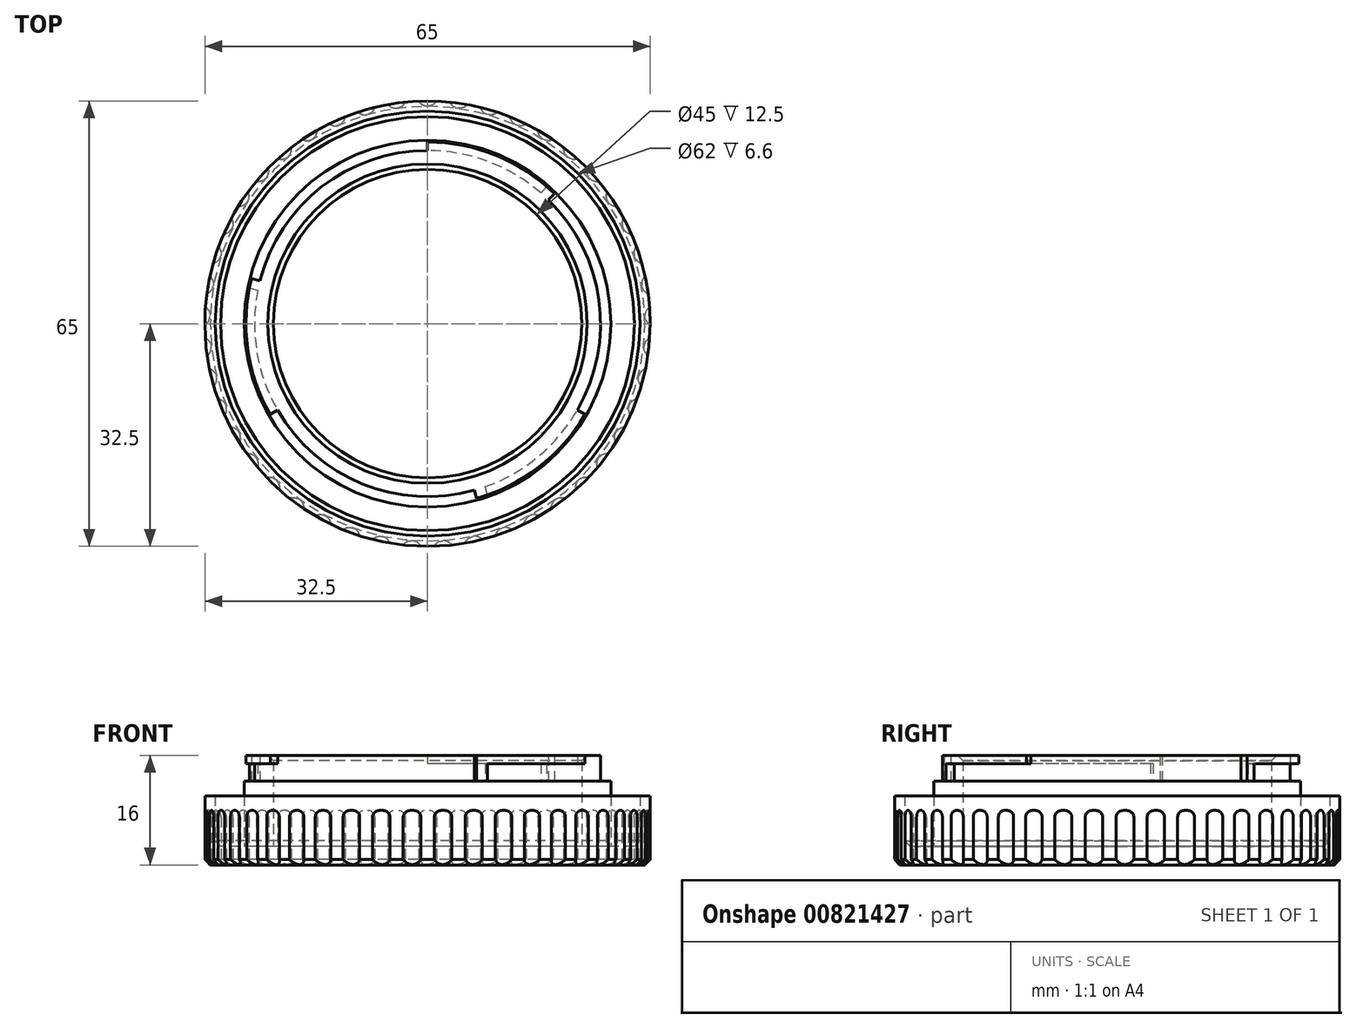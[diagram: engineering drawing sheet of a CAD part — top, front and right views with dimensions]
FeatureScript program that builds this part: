
annotation { "Feature Type Name" : "Feature", "Feature Type Description" : "" }
export const myFeature = defineFeature(function(context is Context, id is Id, definition is map)
    precondition{}
    {
        {
            var Q0;
            Q0=qCreatedBy(makeId("Top.planeOp"),FACE);
            var sketch = newSketch(context, id + "F0", { "sketchPlane" : qUnion([Q0])});
            skCircle(sketch, "E0", {"center": v(0, 0) * mm, "radius": 32.5 * mm});
            skCircle(sketch, "E1", {"center": v(0, 0) * mm, "radius": 31 * mm});
            skCircle(sketch, "E2", {"center": v(0, 0) * mm, "radius": 26.75 * mm});
            skCircle(sketch, "E3", {"center": v(0, 0) * mm, "radius": 25.25 * mm});
            skCircle(sketch, "E4", {"center": v(0, 0) * mm, "radius": 22.5 * mm});
            skCircle(sketch, "E5", {"center": v(0, 0) * mm, "radius": 26.5 * mm});
            skLineSegment(sketch, "E6", {"start": v(0, -3.47) * mm, "end": v(0, 43.61) * mm, "construction": true});
            skLineSegment(sketch, "E7", {"start": v(0, 26.5) * mm, "end": v(0, 25.25) * mm, "construction": true});
            skLineSegment(sketch, "E8", {"start": v(0, 0) * mm, "end": v(34.45, 35.25) * mm, "construction": true});
            skLineSegment(sketch, "E9", {"start": v(18.52, 18.95) * mm, "end": v(17.65, 18.06) * mm});
            skLineSegment(sketch, "E10.1.0", {"start": v(3, 1.74) * mm, "end": v(-37.77, -21.8) * mm, "construction": true});
            skLineSegment(sketch, "E10.1.1", {"start": v(0, 0) * mm, "end": v(-47.75, 12.2) * mm, "construction": true});
            skLineSegment(sketch, "E10.2.0", {"start": v(-3, 1.74) * mm, "end": v(37.77, -21.8) * mm, "construction": true});
            skLineSegment(sketch, "E10.2.1", {"start": v(0, 0) * mm, "end": v(13.3, -47.46) * mm, "construction": true});
            skLineSegment(sketch, "E11", {"start": v(-25.67, 6.56) * mm, "end": v(-24.46, 6.25) * mm});
            skLineSegment(sketch, "E12", {"start": v(-22.95, -13.25) * mm, "end": v(-21.87, -12.62) * mm});
            skLineSegment(sketch, "E13", {"start": v(6.82, -24.31) * mm, "end": v(7.15, -25.52) * mm});
            skLineSegment(sketch, "E14", {"start": v(21.87, -12.63) * mm, "end": v(22.95, -13.25) * mm});
            skCircle(sketch, "E15", {"center": v(0, 33.28) * mm, "radius": 1.52 * mm});
            skCircle(sketch, "E16.1.0", {"center": v(-4.63, 32.95) * mm, "radius": 1.52 * mm});
            skCircle(sketch, "E16.2.0", {"center": v(-9.17, 31.99) * mm, "radius": 1.52 * mm});
            skCircle(sketch, "E16.3.0", {"center": v(-13.53, 30.4) * mm, "radius": 1.52 * mm});
            skCircle(sketch, "E16.4.0", {"center": v(-17.63, 28.22) * mm, "radius": 1.52 * mm});
            skCircle(sketch, "E16.5.0", {"center": v(-21.39, 25.5) * mm, "radius": 1.52 * mm});
            skCircle(sketch, "E16.6.0", {"center": v(-24.73, 22.27) * mm, "radius": 1.52 * mm});
            skCircle(sketch, "E16.7.0", {"center": v(-27.59, 18.6) * mm, "radius": 1.52 * mm});
            skCircle(sketch, "E16.8.0", {"center": v(-29.9, 14.59) * mm, "radius": 1.52 * mm});
            skCircle(sketch, "E16.9.0", {"center": v(-31.65, 10.28) * mm, "radius": 1.52 * mm});
            skCircle(sketch, "E16.10.0", {"center": v(-32.77, 5.78) * mm, "radius": 1.52 * mm});
            skCircle(sketch, "E16.11.0", {"center": v(-33.26, 1.16) * mm, "radius": 1.52 * mm});
            skCircle(sketch, "E16.12.0", {"center": v(-33.1, -3.48) * mm, "radius": 1.52 * mm});
            skCircle(sketch, "E16.13.0", {"center": v(-32.29, -8.05) * mm, "radius": 1.52 * mm});
            skCircle(sketch, "E16.14.0", {"center": v(-30.85, -12.47) * mm, "radius": 1.52 * mm});
            skCircle(sketch, "E16.15.0", {"center": v(-28.82, -16.64) * mm, "radius": 1.52 * mm});
            skCircle(sketch, "E16.16.0", {"center": v(-26.22, -20.49) * mm, "radius": 1.52 * mm});
            skCircle(sketch, "E16.17.0", {"center": v(-23.12, -23.94) * mm, "radius": 1.52 * mm});
            skCircle(sketch, "E16.18.0", {"center": v(-19.56, -26.92) * mm, "radius": 1.52 * mm});
            skCircle(sketch, "E16.19.0", {"center": v(-15.62, -29.38) * mm, "radius": 1.52 * mm});
            skCircle(sketch, "E16.20.0", {"center": v(-11.38, -31.27) * mm, "radius": 1.52 * mm});
            skCircle(sketch, "E16.21.0", {"center": v(-6.92, -32.55) * mm, "radius": 1.52 * mm});
            skCircle(sketch, "E16.22.0", {"center": v(-2.32, -33.2) * mm, "radius": 1.52 * mm});
            skCircle(sketch, "E16.23.0", {"center": v(2.32, -33.2) * mm, "radius": 1.52 * mm});
            skCircle(sketch, "E16.24.0", {"center": v(6.92, -32.55) * mm, "radius": 1.52 * mm});
            skCircle(sketch, "E16.25.0", {"center": v(11.38, -31.27) * mm, "radius": 1.52 * mm});
            skCircle(sketch, "E16.26.0", {"center": v(15.62, -29.38) * mm, "radius": 1.52 * mm});
            skCircle(sketch, "E16.27.0", {"center": v(19.56, -26.92) * mm, "radius": 1.52 * mm});
            skCircle(sketch, "E16.28.0", {"center": v(23.12, -23.94) * mm, "radius": 1.52 * mm});
            skCircle(sketch, "E16.29.0", {"center": v(26.22, -20.49) * mm, "radius": 1.52 * mm});
            skCircle(sketch, "E16.30.0", {"center": v(28.82, -16.64) * mm, "radius": 1.52 * mm});
            skCircle(sketch, "E16.31.0", {"center": v(30.85, -12.47) * mm, "radius": 1.52 * mm});
            skCircle(sketch, "E16.32.0", {"center": v(32.29, -8.05) * mm, "radius": 1.52 * mm});
            skCircle(sketch, "E16.33.0", {"center": v(33.1, -3.48) * mm, "radius": 1.52 * mm});
            skCircle(sketch, "E16.34.0", {"center": v(33.26, 1.16) * mm, "radius": 1.52 * mm});
            skCircle(sketch, "E16.35.0", {"center": v(32.77, 5.78) * mm, "radius": 1.52 * mm});
            skCircle(sketch, "E16.36.0", {"center": v(31.65, 10.28) * mm, "radius": 1.52 * mm});
            skCircle(sketch, "E16.37.0", {"center": v(29.9, 14.59) * mm, "radius": 1.52 * mm});
            skCircle(sketch, "E16.38.0", {"center": v(27.59, 18.6) * mm, "radius": 1.52 * mm});
            skCircle(sketch, "E16.39.0", {"center": v(24.73, 22.27) * mm, "radius": 1.52 * mm});
            skCircle(sketch, "E16.40.0", {"center": v(21.39, 25.5) * mm, "radius": 1.52 * mm});
            skCircle(sketch, "E16.41.0", {"center": v(17.63, 28.22) * mm, "radius": 1.52 * mm});
            skCircle(sketch, "E16.42.0", {"center": v(13.53, 30.4) * mm, "radius": 1.52 * mm});
            skCircle(sketch, "E16.43.0", {"center": v(9.17, 31.99) * mm, "radius": 1.52 * mm});
            skCircle(sketch, "E16.44.0", {"center": v(4.63, 32.95) * mm, "radius": 1.52 * mm});
            skLineSegment(sketch, "E17", {"start": v(0, 25.25) * mm, "end": v(0, 26.5) * mm});
            skLineSegment(sketch, "E18", {"start": v(17.4, 19.98) * mm, "end": v(16.57, 19.05) * mm});
            skLineSegment(sketch, "E19", {"start": v(8.77, -25) * mm, "end": v(8.43, -23.8) * mm});
            skLineSegment(sketch, "E20", {"start": v(-25.97, 5.25) * mm, "end": v(-24.78, 4.86) * mm});
            skSolve(sketch);
        }
        {
            var Q0;
            Q0=makeQuery(id+"F0.imprint","IMPRINT",FACE,{"disambiguationData":[TD([[makeQuery(id+"F0.imprint","IMPRINT",EDGE,{"derivedFrom":sQuery(id+"F0.wireOp",EDGE,"E4")}),-1.0]])]});
            var Q1;
            {var subQ0=sQuery(id+"F0.wireOp",EDGE,"E11");Q1=makeQuery(id+"F0.imprint","IMPRINT",FACE,{"disambiguationData":[TD([[makeQuery(id+"F0.imprint","IMPRINT",EDGE,{"derivedFrom":subQ0}),-1.0]])]});}
            var Q2;
            {var subQ0=sQuery(id+"F0.wireOp",EDGE,"E13");Q2=makeQuery(id+"F0.imprint","IMPRINT",FACE,{"disambiguationData":[TD([[makeQuery(id+"F0.imprint","IMPRINT",EDGE,{"derivedFrom":subQ0}),1.0]])]});}
            var Q3;
            {var subQ0=sQuery(id+"F0.wireOp",EDGE,"E9");Q3=makeQuery(id+"F0.imprint","IMPRINT",FACE,{"disambiguationData":[TD([[makeQuery(id+"F0.imprint","IMPRINT",EDGE,{"derivedFrom":subQ0}),-1.0]])]});}
            extrude(context, id + "F1", {"entities" : qUnion([Q0, Q1, Q2, Q3]), "depth" : 16 * mm, "offsetDistance" : 25 * mm});
        }
        {
            var Q0;
            {var subQ0=sQuery(id+"F0.wireOp",EDGE,"E13");Q0=makeQuery(id+"F0.imprint","IMPRINT",FACE,{"disambiguationData":[TD([[makeQuery(id+"F0.imprint","IMPRINT",EDGE,{"derivedFrom":subQ0}),1.0]])]});}
            var Q1;
            {var subQ0=sQuery(id+"F0.wireOp",EDGE,"E9");Q1=makeQuery(id+"F0.imprint","IMPRINT",FACE,{"disambiguationData":[TD([[makeQuery(id+"F0.imprint","IMPRINT",EDGE,{"derivedFrom":subQ0}),-1.0]])]});}
            var Q2;
            {var subQ0=sQuery(id+"F0.wireOp",EDGE,"E11");Q2=makeQuery(id+"F0.imprint","IMPRINT",FACE,{"disambiguationData":[TD([[makeQuery(id+"F0.imprint","IMPRINT",EDGE,{"derivedFrom":subQ0}),-1.0]])]});}
            var Q3;
            {var subQ0=sQuery(id+"F0.wireOp",EDGE,"E14");Q3=makeQuery(id+"F0.imprint","IMPRINT",FACE,{"disambiguationData":[TD([[makeQuery(id+"F0.imprint","IMPRINT",EDGE,{"derivedFrom":subQ0}),-1.0]])]});}
            var Q4;
            {var subQ0=sQuery(id+"F0.wireOp",EDGE,"E17");Q4=makeQuery(id+"F0.imprint","IMPRINT",FACE,{"disambiguationData":[TD([[makeQuery(id+"F0.imprint","IMPRINT",EDGE,{"derivedFrom":subQ0}),-1.0]])]});}
            var Q5;
            {var subQ0=sQuery(id+"F0.wireOp",EDGE,"E12");Q5=makeQuery(id+"F0.imprint","IMPRINT",FACE,{"disambiguationData":[TD([[makeQuery(id+"F0.imprint","IMPRINT",EDGE,{"derivedFrom":subQ0}),1.0]])]});}
            extrude(context, id + "F2", {"entities" : qUnion([Q0, Q1, Q2, Q3, Q4, Q5]), "operationType" : NewBodyOperationType.ADD, "depth" : 16 * mm, "offsetDistance" : 25 * mm, "hasSecondDirection" : true, "secondDirectionOppositeDirection" : false, "secondDirectionDepth" : 14.8 * mm});
        }
        {
            var Q0;
            Q0=makeQuery(id+"F0.imprint","IMPRINT",FACE,{"disambiguationData":[TD([[makeQuery(id+"F0.imprint","IMPRINT",EDGE,{"derivedFrom":sQuery(id+"F0.wireOp",EDGE,"E2")}),1.0]])]});
            var Q1;
            {var subQ0=sQuery(id+"F0.wireOp",EDGE,"E9");Q1=makeQuery(id+"F0.imprint","IMPRINT",FACE,{"disambiguationData":[TD([[makeQuery(id+"F0.imprint","IMPRINT",EDGE,{"derivedFrom":subQ0}),1.0]])]});}
            var Q2;
            {var subQ0=sQuery(id+"F0.wireOp",EDGE,"E14");Q2=makeQuery(id+"F0.imprint","IMPRINT",FACE,{"disambiguationData":[TD([[makeQuery(id+"F0.imprint","IMPRINT",EDGE,{"derivedFrom":subQ0}),-1.0]])]});}
            var Q3;
            {var subQ0=sQuery(id+"F0.wireOp",EDGE,"E12");Q3=makeQuery(id+"F0.imprint","IMPRINT",FACE,{"disambiguationData":[TD([[makeQuery(id+"F0.imprint","IMPRINT",EDGE,{"derivedFrom":subQ0}),-1.0]])]});}
            var Q4;
            {var subQ0=sQuery(id+"F0.wireOp",EDGE,"E11");Q4=makeQuery(id+"F0.imprint","IMPRINT",FACE,{"disambiguationData":[TD([[makeQuery(id+"F0.imprint","IMPRINT",EDGE,{"derivedFrom":subQ0}),1.0]])]});}
            var Q5;
            {var subQ0=sQuery(id+"F0.wireOp",EDGE,"E12");Q5=makeQuery(id+"F0.imprint","IMPRINT",FACE,{"disambiguationData":[TD([[makeQuery(id+"F0.imprint","IMPRINT",EDGE,{"derivedFrom":subQ0}),1.0]])]});}
            var Q6;
            {var subQ0=sQuery(id+"F0.wireOp",EDGE,"E17");Q6=makeQuery(id+"F0.imprint","IMPRINT",FACE,{"disambiguationData":[TD([[makeQuery(id+"F0.imprint","IMPRINT",EDGE,{"derivedFrom":subQ0}),-1.0]])]});}
            extrude(context, id + "F3", {"entities" : qUnion([Q0, Q1, Q2, Q3, Q4, Q5, Q6]), "operationType" : NewBodyOperationType.ADD, "depth" : 12.2 * mm, "offsetDistance" : 25 * mm});
        }
        {
            var Q0;
            Q0=makeQuery(id+"F0.imprint","IMPRINT",FACE,{"disambiguationData":[TD([[makeQuery(id+"F0.imprint","IMPRINT",EDGE,{"derivedFrom":sQuery(id+"F0.wireOp",EDGE,"E1")}),1.0]])]});
            var Q1;
            Q1=makeQuery(id+"F0.imprint","IMPRINT",FACE,{"disambiguationData":[TD([[makeQuery(id+"F0.imprint","IMPRINT",EDGE,{"derivedFrom":sQuery(id+"F0.wireOp",EDGE,"E4")}),1.0]])]});
            extrude(context, id + "F4", {"entities" : qUnion([Q0, Q1]), "operationType" : NewBodyOperationType.ADD, "depth" : 2.7 * mm, "offsetDistance" : 25 * mm});
        }
        {
            var Q0;
            {var subQ0=sQuery(id+"F0.wireOp",EDGE,"E16.36.0");var subQ1=sQuery(id+"F0.wireOp",EDGE,"E0");var subQ2=makeQuery(id+"F0.imprint","INTERSECT",VERTEX,{"disambiguationData":[OD(0.0)],"derivedFrom":[subQ1,subQ0]});Q0=makeQuery(id+"F0.imprint","IMPRINT",FACE,{"disambiguationData":[TD([[makeQuery(id+"F0.imprint","IMPRINT",EDGE,{"disambiguationData":[TD([[subQ2,-1.0]])],"derivedFrom":subQ1}),1.0]])]});}
            var Q1;
            Q1=makeQuery(id+"F0.imprint","IMPRINT",FACE,{"disambiguationData":[TD([[makeQuery(id+"F0.imprint","IMPRINT",EDGE,{"derivedFrom":sQuery(id+"F0.wireOp",EDGE,"E1")}),-1.0]])]});
            var Q2;
            {var subQ0=sQuery(id+"F0.wireOp",EDGE,"E16.35.0");var subQ1=sQuery(id+"F0.wireOp",EDGE,"E0");var subQ2=makeQuery(id+"F0.imprint","INTERSECT",VERTEX,{"disambiguationData":[OD(0.0)],"derivedFrom":[subQ1,subQ0]});Q2=makeQuery(id+"F0.imprint","IMPRINT",FACE,{"disambiguationData":[TD([[makeQuery(id+"F0.imprint","IMPRINT",EDGE,{"disambiguationData":[TD([[subQ2,-1.0]])],"derivedFrom":subQ1}),1.0]])]});}
            var Q3;
            {var subQ0=sQuery(id+"F0.wireOp",EDGE,"E16.37.0");var subQ1=sQuery(id+"F0.wireOp",EDGE,"E0");var subQ2=makeQuery(id+"F0.imprint","INTERSECT",VERTEX,{"disambiguationData":[OD(0.0)],"derivedFrom":[subQ1,subQ0]});Q3=makeQuery(id+"F0.imprint","IMPRINT",FACE,{"disambiguationData":[TD([[makeQuery(id+"F0.imprint","IMPRINT",EDGE,{"disambiguationData":[TD([[subQ2,-1.0]])],"derivedFrom":subQ1}),1.0]])]});}
            var Q4;
            {var subQ0=sQuery(id+"F0.wireOp",EDGE,"E16.38.0");var subQ1=sQuery(id+"F0.wireOp",EDGE,"E0");var subQ2=makeQuery(id+"F0.imprint","INTERSECT",VERTEX,{"disambiguationData":[OD(0.0)],"derivedFrom":[subQ1,subQ0]});Q4=makeQuery(id+"F0.imprint","IMPRINT",FACE,{"disambiguationData":[TD([[makeQuery(id+"F0.imprint","IMPRINT",EDGE,{"disambiguationData":[TD([[subQ2,-1.0]])],"derivedFrom":subQ1}),1.0]])]});}
            var Q5;
            {var subQ0=sQuery(id+"F0.wireOp",EDGE,"E16.39.0");var subQ1=sQuery(id+"F0.wireOp",EDGE,"E0");var subQ2=makeQuery(id+"F0.imprint","INTERSECT",VERTEX,{"disambiguationData":[OD(0.0)],"derivedFrom":[subQ1,subQ0]});Q5=makeQuery(id+"F0.imprint","IMPRINT",FACE,{"disambiguationData":[TD([[makeQuery(id+"F0.imprint","IMPRINT",EDGE,{"disambiguationData":[TD([[subQ2,-1.0]])],"derivedFrom":subQ1}),1.0]])]});}
            var Q6;
            {var subQ0=sQuery(id+"F0.wireOp",EDGE,"E16.40.0");var subQ1=sQuery(id+"F0.wireOp",EDGE,"E0");var subQ2=makeQuery(id+"F0.imprint","INTERSECT",VERTEX,{"disambiguationData":[OD(0.0)],"derivedFrom":[subQ1,subQ0]});Q6=makeQuery(id+"F0.imprint","IMPRINT",FACE,{"disambiguationData":[TD([[makeQuery(id+"F0.imprint","IMPRINT",EDGE,{"disambiguationData":[TD([[subQ2,-1.0]])],"derivedFrom":subQ1}),1.0]])]});}
            var Q7;
            {var subQ0=sQuery(id+"F0.wireOp",EDGE,"E16.41.0");var subQ1=sQuery(id+"F0.wireOp",EDGE,"E0");var subQ2=makeQuery(id+"F0.imprint","INTERSECT",VERTEX,{"disambiguationData":[OD(0.0)],"derivedFrom":[subQ1,subQ0]});Q7=makeQuery(id+"F0.imprint","IMPRINT",FACE,{"disambiguationData":[TD([[makeQuery(id+"F0.imprint","IMPRINT",EDGE,{"disambiguationData":[TD([[subQ2,-1.0]])],"derivedFrom":subQ1}),1.0]])]});}
            var Q8;
            {var subQ0=sQuery(id+"F0.wireOp",EDGE,"E16.42.0");var subQ1=sQuery(id+"F0.wireOp",EDGE,"E0");var subQ2=makeQuery(id+"F0.imprint","INTERSECT",VERTEX,{"disambiguationData":[OD(0.0)],"derivedFrom":[subQ1,subQ0]});Q8=makeQuery(id+"F0.imprint","IMPRINT",FACE,{"disambiguationData":[TD([[makeQuery(id+"F0.imprint","IMPRINT",EDGE,{"disambiguationData":[TD([[subQ2,-1.0]])],"derivedFrom":subQ1}),1.0]])]});}
            var Q9;
            {var subQ0=sQuery(id+"F0.wireOp",EDGE,"E16.43.0");var subQ1=sQuery(id+"F0.wireOp",EDGE,"E0");var subQ2=makeQuery(id+"F0.imprint","INTERSECT",VERTEX,{"disambiguationData":[OD(0.0)],"derivedFrom":[subQ1,subQ0]});Q9=makeQuery(id+"F0.imprint","IMPRINT",FACE,{"disambiguationData":[TD([[makeQuery(id+"F0.imprint","IMPRINT",EDGE,{"disambiguationData":[TD([[subQ2,-1.0]])],"derivedFrom":subQ1}),1.0]])]});}
            var Q10;
            {var subQ0=sQuery(id+"F0.wireOp",EDGE,"E16.44.0");var subQ1=sQuery(id+"F0.wireOp",EDGE,"E0");var subQ2=makeQuery(id+"F0.imprint","INTERSECT",VERTEX,{"disambiguationData":[OD(0.0)],"derivedFrom":[subQ1,subQ0]});Q10=makeQuery(id+"F0.imprint","IMPRINT",FACE,{"disambiguationData":[TD([[makeQuery(id+"F0.imprint","IMPRINT",EDGE,{"disambiguationData":[TD([[subQ2,-1.0]])],"derivedFrom":subQ1}),1.0]])]});}
            var Q11;
            {var subQ0=sQuery(id+"F0.wireOp",EDGE,"E15");var subQ1=sQuery(id+"F0.wireOp",EDGE,"E0");var subQ2=makeQuery(id+"F0.imprint","INTERSECT",VERTEX,{"disambiguationData":[OD(0.0)],"derivedFrom":[subQ1,subQ0]});Q11=makeQuery(id+"F0.imprint","IMPRINT",FACE,{"disambiguationData":[TD([[makeQuery(id+"F0.imprint","IMPRINT",EDGE,{"disambiguationData":[TD([[subQ2,-1.0]])],"derivedFrom":subQ1}),1.0]])]});}
            var Q12;
            {var subQ0=sQuery(id+"F0.wireOp",EDGE,"E16.1.0");var subQ1=sQuery(id+"F0.wireOp",EDGE,"E0");var subQ2=makeQuery(id+"F0.imprint","INTERSECT",VERTEX,{"disambiguationData":[OD(0.0)],"derivedFrom":[subQ1,subQ0]});Q12=makeQuery(id+"F0.imprint","IMPRINT",FACE,{"disambiguationData":[TD([[makeQuery(id+"F0.imprint","IMPRINT",EDGE,{"disambiguationData":[TD([[subQ2,-1.0]])],"derivedFrom":subQ1}),1.0]])]});}
            var Q13;
            {var subQ0=sQuery(id+"F0.wireOp",EDGE,"E16.2.0");var subQ1=sQuery(id+"F0.wireOp",EDGE,"E0");var subQ2=makeQuery(id+"F0.imprint","INTERSECT",VERTEX,{"disambiguationData":[OD(0.0)],"derivedFrom":[subQ1,subQ0]});Q13=makeQuery(id+"F0.imprint","IMPRINT",FACE,{"disambiguationData":[TD([[makeQuery(id+"F0.imprint","IMPRINT",EDGE,{"disambiguationData":[TD([[subQ2,-1.0]])],"derivedFrom":subQ1}),1.0]])]});}
            var Q14;
            {var subQ0=sQuery(id+"F0.wireOp",EDGE,"E16.3.0");var subQ1=sQuery(id+"F0.wireOp",EDGE,"E0");var subQ2=makeQuery(id+"F0.imprint","INTERSECT",VERTEX,{"disambiguationData":[OD(0.0)],"derivedFrom":[subQ1,subQ0]});Q14=makeQuery(id+"F0.imprint","IMPRINT",FACE,{"disambiguationData":[TD([[makeQuery(id+"F0.imprint","IMPRINT",EDGE,{"disambiguationData":[TD([[subQ2,-1.0]])],"derivedFrom":subQ1}),1.0]])]});}
            var Q15;
            {var subQ0=sQuery(id+"F0.wireOp",EDGE,"E16.4.0");var subQ1=sQuery(id+"F0.wireOp",EDGE,"E0");var subQ2=makeQuery(id+"F0.imprint","INTERSECT",VERTEX,{"disambiguationData":[OD(0.0)],"derivedFrom":[subQ1,subQ0]});Q15=makeQuery(id+"F0.imprint","IMPRINT",FACE,{"disambiguationData":[TD([[makeQuery(id+"F0.imprint","IMPRINT",EDGE,{"disambiguationData":[TD([[subQ2,-1.0]])],"derivedFrom":subQ1}),1.0]])]});}
            var Q16;
            {var subQ0=sQuery(id+"F0.wireOp",EDGE,"E16.5.0");var subQ1=sQuery(id+"F0.wireOp",EDGE,"E0");var subQ2=makeQuery(id+"F0.imprint","INTERSECT",VERTEX,{"disambiguationData":[OD(0.0)],"derivedFrom":[subQ1,subQ0]});Q16=makeQuery(id+"F0.imprint","IMPRINT",FACE,{"disambiguationData":[TD([[makeQuery(id+"F0.imprint","IMPRINT",EDGE,{"disambiguationData":[TD([[subQ2,-1.0]])],"derivedFrom":subQ1}),1.0]])]});}
            var Q17;
            {var subQ0=sQuery(id+"F0.wireOp",EDGE,"E16.6.0");var subQ1=sQuery(id+"F0.wireOp",EDGE,"E0");var subQ2=makeQuery(id+"F0.imprint","INTERSECT",VERTEX,{"disambiguationData":[OD(0.0)],"derivedFrom":[subQ1,subQ0]});Q17=makeQuery(id+"F0.imprint","IMPRINT",FACE,{"disambiguationData":[TD([[makeQuery(id+"F0.imprint","IMPRINT",EDGE,{"disambiguationData":[TD([[subQ2,-1.0]])],"derivedFrom":subQ1}),1.0]])]});}
            var Q18;
            {var subQ0=sQuery(id+"F0.wireOp",EDGE,"E16.11.0");var subQ1=sQuery(id+"F0.wireOp",EDGE,"E0");var subQ2=makeQuery(id+"F0.imprint","INTERSECT",VERTEX,{"disambiguationData":[OD(0.0)],"derivedFrom":[subQ1,subQ0]});Q18=makeQuery(id+"F0.imprint","IMPRINT",FACE,{"disambiguationData":[TD([[makeQuery(id+"F0.imprint","IMPRINT",EDGE,{"disambiguationData":[TD([[subQ2,-1.0]])],"derivedFrom":subQ1}),1.0]])]});}
            var Q19;
            {var subQ0=sQuery(id+"F0.wireOp",EDGE,"E16.10.0");var subQ1=sQuery(id+"F0.wireOp",EDGE,"E0");var subQ2=makeQuery(id+"F0.imprint","INTERSECT",VERTEX,{"disambiguationData":[OD(0.0)],"derivedFrom":[subQ1,subQ0]});Q19=makeQuery(id+"F0.imprint","IMPRINT",FACE,{"disambiguationData":[TD([[makeQuery(id+"F0.imprint","IMPRINT",EDGE,{"disambiguationData":[TD([[subQ2,-1.0]])],"derivedFrom":subQ1}),1.0]])]});}
            var Q20;
            {var subQ0=sQuery(id+"F0.wireOp",EDGE,"E16.9.0");var subQ1=sQuery(id+"F0.wireOp",EDGE,"E0");var subQ2=makeQuery(id+"F0.imprint","INTERSECT",VERTEX,{"disambiguationData":[OD(0.0)],"derivedFrom":[subQ1,subQ0]});Q20=makeQuery(id+"F0.imprint","IMPRINT",FACE,{"disambiguationData":[TD([[makeQuery(id+"F0.imprint","IMPRINT",EDGE,{"disambiguationData":[TD([[subQ2,-1.0]])],"derivedFrom":subQ1}),1.0]])]});}
            var Q21;
            {var subQ0=sQuery(id+"F0.wireOp",EDGE,"E16.12.0");var subQ1=sQuery(id+"F0.wireOp",EDGE,"E0");var subQ2=makeQuery(id+"F0.imprint","INTERSECT",VERTEX,{"disambiguationData":[OD(0.0)],"derivedFrom":[subQ1,subQ0]});Q21=makeQuery(id+"F0.imprint","IMPRINT",FACE,{"disambiguationData":[TD([[makeQuery(id+"F0.imprint","IMPRINT",EDGE,{"disambiguationData":[TD([[subQ2,-1.0]])],"derivedFrom":subQ1}),1.0]])]});}
            var Q22;
            {var subQ0=sQuery(id+"F0.wireOp",EDGE,"E16.7.0");var subQ1=sQuery(id+"F0.wireOp",EDGE,"E0");var subQ2=makeQuery(id+"F0.imprint","INTERSECT",VERTEX,{"disambiguationData":[OD(0.0)],"derivedFrom":[subQ1,subQ0]});Q22=makeQuery(id+"F0.imprint","IMPRINT",FACE,{"disambiguationData":[TD([[makeQuery(id+"F0.imprint","IMPRINT",EDGE,{"disambiguationData":[TD([[subQ2,-1.0]])],"derivedFrom":subQ1}),1.0]])]});}
            var Q23;
            {var subQ0=sQuery(id+"F0.wireOp",EDGE,"E16.8.0");var subQ1=sQuery(id+"F0.wireOp",EDGE,"E0");var subQ2=makeQuery(id+"F0.imprint","INTERSECT",VERTEX,{"disambiguationData":[OD(0.0)],"derivedFrom":[subQ1,subQ0]});Q23=makeQuery(id+"F0.imprint","IMPRINT",FACE,{"disambiguationData":[TD([[makeQuery(id+"F0.imprint","IMPRINT",EDGE,{"disambiguationData":[TD([[subQ2,-1.0]])],"derivedFrom":subQ1}),1.0]])]});}
            var Q24;
            {var subQ0=sQuery(id+"F0.wireOp",EDGE,"E16.13.0");var subQ1=sQuery(id+"F0.wireOp",EDGE,"E0");var subQ2=makeQuery(id+"F0.imprint","INTERSECT",VERTEX,{"disambiguationData":[OD(0.0)],"derivedFrom":[subQ1,subQ0]});Q24=makeQuery(id+"F0.imprint","IMPRINT",FACE,{"disambiguationData":[TD([[makeQuery(id+"F0.imprint","IMPRINT",EDGE,{"disambiguationData":[TD([[subQ2,-1.0]])],"derivedFrom":subQ1}),1.0]])]});}
            var Q25;
            {var subQ0=sQuery(id+"F0.wireOp",EDGE,"E16.14.0");var subQ1=sQuery(id+"F0.wireOp",EDGE,"E0");var subQ2=makeQuery(id+"F0.imprint","INTERSECT",VERTEX,{"disambiguationData":[OD(0.0)],"derivedFrom":[subQ1,subQ0]});Q25=makeQuery(id+"F0.imprint","IMPRINT",FACE,{"disambiguationData":[TD([[makeQuery(id+"F0.imprint","IMPRINT",EDGE,{"disambiguationData":[TD([[subQ2,-1.0]])],"derivedFrom":subQ1}),1.0]])]});}
            var Q26;
            {var subQ0=sQuery(id+"F0.wireOp",EDGE,"E16.15.0");var subQ1=sQuery(id+"F0.wireOp",EDGE,"E0");var subQ2=makeQuery(id+"F0.imprint","INTERSECT",VERTEX,{"disambiguationData":[OD(0.0)],"derivedFrom":[subQ1,subQ0]});Q26=makeQuery(id+"F0.imprint","IMPRINT",FACE,{"disambiguationData":[TD([[makeQuery(id+"F0.imprint","IMPRINT",EDGE,{"disambiguationData":[TD([[subQ2,-1.0]])],"derivedFrom":subQ1}),1.0]])]});}
            var Q27;
            {var subQ0=sQuery(id+"F0.wireOp",EDGE,"E16.16.0");var subQ1=sQuery(id+"F0.wireOp",EDGE,"E0");var subQ2=makeQuery(id+"F0.imprint","INTERSECT",VERTEX,{"disambiguationData":[OD(0.0)],"derivedFrom":[subQ1,subQ0]});Q27=makeQuery(id+"F0.imprint","IMPRINT",FACE,{"disambiguationData":[TD([[makeQuery(id+"F0.imprint","IMPRINT",EDGE,{"disambiguationData":[TD([[subQ2,-1.0]])],"derivedFrom":subQ1}),1.0]])]});}
            var Q28;
            {var subQ0=sQuery(id+"F0.wireOp",EDGE,"E16.17.0");var subQ1=sQuery(id+"F0.wireOp",EDGE,"E0");var subQ2=makeQuery(id+"F0.imprint","INTERSECT",VERTEX,{"disambiguationData":[OD(0.0)],"derivedFrom":[subQ1,subQ0]});Q28=makeQuery(id+"F0.imprint","IMPRINT",FACE,{"disambiguationData":[TD([[makeQuery(id+"F0.imprint","IMPRINT",EDGE,{"disambiguationData":[TD([[subQ2,-1.0]])],"derivedFrom":subQ1}),1.0]])]});}
            var Q29;
            {var subQ0=sQuery(id+"F0.wireOp",EDGE,"E16.18.0");var subQ1=sQuery(id+"F0.wireOp",EDGE,"E0");var subQ2=makeQuery(id+"F0.imprint","INTERSECT",VERTEX,{"disambiguationData":[OD(0.0)],"derivedFrom":[subQ1,subQ0]});Q29=makeQuery(id+"F0.imprint","IMPRINT",FACE,{"disambiguationData":[TD([[makeQuery(id+"F0.imprint","IMPRINT",EDGE,{"disambiguationData":[TD([[subQ2,-1.0]])],"derivedFrom":subQ1}),1.0]])]});}
            var Q30;
            {var subQ0=sQuery(id+"F0.wireOp",EDGE,"E16.19.0");var subQ1=sQuery(id+"F0.wireOp",EDGE,"E0");var subQ2=makeQuery(id+"F0.imprint","INTERSECT",VERTEX,{"disambiguationData":[OD(0.0)],"derivedFrom":[subQ1,subQ0]});Q30=makeQuery(id+"F0.imprint","IMPRINT",FACE,{"disambiguationData":[TD([[makeQuery(id+"F0.imprint","IMPRINT",EDGE,{"disambiguationData":[TD([[subQ2,-1.0]])],"derivedFrom":subQ1}),1.0]])]});}
            var Q31;
            {var subQ0=sQuery(id+"F0.wireOp",EDGE,"E16.20.0");var subQ1=sQuery(id+"F0.wireOp",EDGE,"E0");var subQ2=makeQuery(id+"F0.imprint","INTERSECT",VERTEX,{"disambiguationData":[OD(0.0)],"derivedFrom":[subQ1,subQ0]});Q31=makeQuery(id+"F0.imprint","IMPRINT",FACE,{"disambiguationData":[TD([[makeQuery(id+"F0.imprint","IMPRINT",EDGE,{"disambiguationData":[TD([[subQ2,-1.0]])],"derivedFrom":subQ1}),1.0]])]});}
            var Q32;
            {var subQ0=sQuery(id+"F0.wireOp",EDGE,"E16.21.0");var subQ1=sQuery(id+"F0.wireOp",EDGE,"E0");var subQ2=makeQuery(id+"F0.imprint","INTERSECT",VERTEX,{"disambiguationData":[OD(0.0)],"derivedFrom":[subQ1,subQ0]});Q32=makeQuery(id+"F0.imprint","IMPRINT",FACE,{"disambiguationData":[TD([[makeQuery(id+"F0.imprint","IMPRINT",EDGE,{"disambiguationData":[TD([[subQ2,-1.0]])],"derivedFrom":subQ1}),1.0]])]});}
            var Q33;
            {var subQ0=sQuery(id+"F0.wireOp",EDGE,"E16.22.0");var subQ1=sQuery(id+"F0.wireOp",EDGE,"E0");var subQ2=makeQuery(id+"F0.imprint","INTERSECT",VERTEX,{"disambiguationData":[OD(0.0)],"derivedFrom":[subQ1,subQ0]});Q33=makeQuery(id+"F0.imprint","IMPRINT",FACE,{"disambiguationData":[TD([[makeQuery(id+"F0.imprint","IMPRINT",EDGE,{"disambiguationData":[TD([[subQ2,-1.0]])],"derivedFrom":subQ1}),1.0]])]});}
            var Q34;
            {var subQ0=sQuery(id+"F0.wireOp",EDGE,"E16.23.0");var subQ1=sQuery(id+"F0.wireOp",EDGE,"E0");var subQ2=makeQuery(id+"F0.imprint","INTERSECT",VERTEX,{"disambiguationData":[OD(0.0)],"derivedFrom":[subQ1,subQ0]});Q34=makeQuery(id+"F0.imprint","IMPRINT",FACE,{"disambiguationData":[TD([[makeQuery(id+"F0.imprint","IMPRINT",EDGE,{"disambiguationData":[TD([[subQ2,-1.0]])],"derivedFrom":subQ1}),1.0]])]});}
            var Q35;
            {var subQ0=sQuery(id+"F0.wireOp",EDGE,"E16.24.0");var subQ1=sQuery(id+"F0.wireOp",EDGE,"E0");var subQ2=makeQuery(id+"F0.imprint","INTERSECT",VERTEX,{"disambiguationData":[OD(0.0)],"derivedFrom":[subQ1,subQ0]});Q35=makeQuery(id+"F0.imprint","IMPRINT",FACE,{"disambiguationData":[TD([[makeQuery(id+"F0.imprint","IMPRINT",EDGE,{"disambiguationData":[TD([[subQ2,-1.0]])],"derivedFrom":subQ1}),1.0]])]});}
            var Q36;
            {var subQ0=sQuery(id+"F0.wireOp",EDGE,"E16.25.0");var subQ1=sQuery(id+"F0.wireOp",EDGE,"E0");var subQ2=makeQuery(id+"F0.imprint","INTERSECT",VERTEX,{"disambiguationData":[OD(0.0)],"derivedFrom":[subQ1,subQ0]});Q36=makeQuery(id+"F0.imprint","IMPRINT",FACE,{"disambiguationData":[TD([[makeQuery(id+"F0.imprint","IMPRINT",EDGE,{"disambiguationData":[TD([[subQ2,-1.0]])],"derivedFrom":subQ1}),1.0]])]});}
            var Q37;
            {var subQ0=sQuery(id+"F0.wireOp",EDGE,"E16.26.0");var subQ1=sQuery(id+"F0.wireOp",EDGE,"E0");var subQ2=makeQuery(id+"F0.imprint","INTERSECT",VERTEX,{"disambiguationData":[OD(0.0)],"derivedFrom":[subQ1,subQ0]});Q37=makeQuery(id+"F0.imprint","IMPRINT",FACE,{"disambiguationData":[TD([[makeQuery(id+"F0.imprint","IMPRINT",EDGE,{"disambiguationData":[TD([[subQ2,-1.0]])],"derivedFrom":subQ1}),1.0]])]});}
            var Q38;
            {var subQ0=sQuery(id+"F0.wireOp",EDGE,"E16.27.0");var subQ1=sQuery(id+"F0.wireOp",EDGE,"E0");var subQ2=makeQuery(id+"F0.imprint","INTERSECT",VERTEX,{"disambiguationData":[OD(0.0)],"derivedFrom":[subQ1,subQ0]});Q38=makeQuery(id+"F0.imprint","IMPRINT",FACE,{"disambiguationData":[TD([[makeQuery(id+"F0.imprint","IMPRINT",EDGE,{"disambiguationData":[TD([[subQ2,-1.0]])],"derivedFrom":subQ1}),1.0]])]});}
            var Q39;
            {var subQ0=sQuery(id+"F0.wireOp",EDGE,"E16.32.0");var subQ1=sQuery(id+"F0.wireOp",EDGE,"E0");var subQ2=makeQuery(id+"F0.imprint","INTERSECT",VERTEX,{"disambiguationData":[OD(0.0)],"derivedFrom":[subQ1,subQ0]});Q39=makeQuery(id+"F0.imprint","IMPRINT",FACE,{"disambiguationData":[TD([[makeQuery(id+"F0.imprint","IMPRINT",EDGE,{"disambiguationData":[TD([[subQ2,-1.0]])],"derivedFrom":subQ1}),1.0]])]});}
            var Q40;
            {var subQ0=sQuery(id+"F0.wireOp",EDGE,"E16.31.0");var subQ1=sQuery(id+"F0.wireOp",EDGE,"E0");var subQ2=makeQuery(id+"F0.imprint","INTERSECT",VERTEX,{"disambiguationData":[OD(0.0)],"derivedFrom":[subQ1,subQ0]});Q40=makeQuery(id+"F0.imprint","IMPRINT",FACE,{"disambiguationData":[TD([[makeQuery(id+"F0.imprint","IMPRINT",EDGE,{"disambiguationData":[TD([[subQ2,-1.0]])],"derivedFrom":subQ1}),1.0]])]});}
            var Q41;
            {var subQ0=sQuery(id+"F0.wireOp",EDGE,"E16.30.0");var subQ1=sQuery(id+"F0.wireOp",EDGE,"E0");var subQ2=makeQuery(id+"F0.imprint","INTERSECT",VERTEX,{"disambiguationData":[OD(0.0)],"derivedFrom":[subQ1,subQ0]});Q41=makeQuery(id+"F0.imprint","IMPRINT",FACE,{"disambiguationData":[TD([[makeQuery(id+"F0.imprint","IMPRINT",EDGE,{"disambiguationData":[TD([[subQ2,-1.0]])],"derivedFrom":subQ1}),1.0]])]});}
            var Q42;
            {var subQ0=sQuery(id+"F0.wireOp",EDGE,"E16.28.0");var subQ1=sQuery(id+"F0.wireOp",EDGE,"E0");var subQ2=makeQuery(id+"F0.imprint","INTERSECT",VERTEX,{"disambiguationData":[OD(0.0)],"derivedFrom":[subQ1,subQ0]});Q42=makeQuery(id+"F0.imprint","IMPRINT",FACE,{"disambiguationData":[TD([[makeQuery(id+"F0.imprint","IMPRINT",EDGE,{"disambiguationData":[TD([[subQ2,-1.0]])],"derivedFrom":subQ1}),1.0]])]});}
            var Q43;
            {var subQ0=sQuery(id+"F0.wireOp",EDGE,"E16.29.0");var subQ1=sQuery(id+"F0.wireOp",EDGE,"E0");var subQ2=makeQuery(id+"F0.imprint","INTERSECT",VERTEX,{"disambiguationData":[OD(0.0)],"derivedFrom":[subQ1,subQ0]});Q43=makeQuery(id+"F0.imprint","IMPRINT",FACE,{"disambiguationData":[TD([[makeQuery(id+"F0.imprint","IMPRINT",EDGE,{"disambiguationData":[TD([[subQ2,-1.0]])],"derivedFrom":subQ1}),1.0]])]});}
            var Q44;
            {var subQ0=sQuery(id+"F0.wireOp",EDGE,"E16.34.0");var subQ1=sQuery(id+"F0.wireOp",EDGE,"E0");var subQ2=makeQuery(id+"F0.imprint","INTERSECT",VERTEX,{"disambiguationData":[OD(0.0)],"derivedFrom":[subQ1,subQ0]});Q44=makeQuery(id+"F0.imprint","IMPRINT",FACE,{"disambiguationData":[TD([[makeQuery(id+"F0.imprint","IMPRINT",EDGE,{"disambiguationData":[TD([[subQ2,1.0]])],"derivedFrom":subQ1}),1.0]])]});}
            var Q45;
            {var subQ0=sQuery(id+"F0.wireOp",EDGE,"E16.33.0");var subQ1=sQuery(id+"F0.wireOp",EDGE,"E0");var subQ2=makeQuery(id+"F0.imprint","INTERSECT",VERTEX,{"disambiguationData":[OD(0.0)],"derivedFrom":[subQ1,subQ0]});Q45=makeQuery(id+"F0.imprint","IMPRINT",FACE,{"disambiguationData":[TD([[makeQuery(id+"F0.imprint","IMPRINT",EDGE,{"disambiguationData":[TD([[subQ2,-1.0]])],"derivedFrom":subQ1}),1.0]])]});}
            extrude(context, id + "F5", {"entities" : qUnion([Q0, Q1, Q2, Q3, Q4, Q5, Q6, Q7, Q8, Q9, Q10, Q11, Q12, Q13, Q14, Q15, Q16, Q17, Q18, Q19, Q20, Q21, Q22, Q23, Q24, Q25, Q26, Q27, Q28, Q29, Q30, Q31, Q32, Q33, Q34, Q35, Q36, Q37, Q38, Q39, Q40, Q41, Q42, Q43, Q44, Q45]), "operationType" : NewBodyOperationType.ADD, "depth" : 10.1 * mm, "offsetDistance" : 25 * mm, "hasSecondDirection" : true, "secondDirectionOppositeDirection" : false, "secondDirectionDepth" : 8 * mm});
        }
        {
            var Q0;
            Q0=makeQuery(id+"F0.imprint","IMPRINT",FACE,{"disambiguationData":[TD([[makeQuery(id+"F0.imprint","IMPRINT",EDGE,{"derivedFrom":sQuery(id+"F0.wireOp",EDGE,"E1")}),-1.0]])]});
            extrude(context, id + "F6", {"entities" : qUnion([Q0]), "operationType" : NewBodyOperationType.ADD, "depth" : 10 * mm, "offsetDistance" : 25 * mm});
        }
        {
            var Q0;
            Q0=makeQuery(id+"F6.boolean.opBoolean","INTERSECT",EDGE,{"derivedFrom":[makeQuery(id+"F5.opExtrude","CAP_FACE",FACE,{"disambiguationData":[OSD([sQuery(id+"F0.wireOp",EDGE,"E0"),sQuery(id+"F0.wireOp",EDGE,"E1")])],"isStart":true}),makeQuery(id+"F6.opExtrude","SWEPT_FACE",FACE,{"disambiguationData":[OSD([sQuery(id+"F0.wireOp",EDGE,"E16.14.0")])]})]});
            var Q1;
            Q1=makeQuery(id+"F6.boolean.opBoolean","INTERSECT",EDGE,{"derivedFrom":[makeQuery(id+"F5.opExtrude","CAP_FACE",FACE,{"disambiguationData":[OSD([sQuery(id+"F0.wireOp",EDGE,"E0"),sQuery(id+"F0.wireOp",EDGE,"E1")])],"isStart":true}),makeQuery(id+"F6.opExtrude","SWEPT_FACE",FACE,{"disambiguationData":[OSD([sQuery(id+"F0.wireOp",EDGE,"E16.13.0")])]})]});
            var Q2;
            Q2=makeQuery(id+"F6.boolean.opBoolean","INTERSECT",EDGE,{"derivedFrom":[makeQuery(id+"F5.opExtrude","CAP_FACE",FACE,{"disambiguationData":[OSD([sQuery(id+"F0.wireOp",EDGE,"E0"),sQuery(id+"F0.wireOp",EDGE,"E1")])],"isStart":true}),makeQuery(id+"F6.opExtrude","SWEPT_FACE",FACE,{"disambiguationData":[OSD([sQuery(id+"F0.wireOp",EDGE,"E16.12.0")])]})]});
            var Q3;
            Q3=makeQuery(id+"F6.boolean.opBoolean","INTERSECT",EDGE,{"derivedFrom":[makeQuery(id+"F5.opExtrude","CAP_FACE",FACE,{"disambiguationData":[OSD([sQuery(id+"F0.wireOp",EDGE,"E0"),sQuery(id+"F0.wireOp",EDGE,"E1")])],"isStart":true}),makeQuery(id+"F6.opExtrude","SWEPT_FACE",FACE,{"disambiguationData":[OSD([sQuery(id+"F0.wireOp",EDGE,"E16.11.0")])]})]});
            var Q4;
            Q4=makeQuery(id+"F6.boolean.opBoolean","INTERSECT",EDGE,{"derivedFrom":[makeQuery(id+"F5.opExtrude","CAP_FACE",FACE,{"disambiguationData":[OSD([sQuery(id+"F0.wireOp",EDGE,"E0"),sQuery(id+"F0.wireOp",EDGE,"E1")])],"isStart":true}),makeQuery(id+"F6.opExtrude","SWEPT_FACE",FACE,{"disambiguationData":[OSD([sQuery(id+"F0.wireOp",EDGE,"E16.10.0")])]})]});
            var Q5;
            Q5=makeQuery(id+"F6.boolean.opBoolean","INTERSECT",EDGE,{"derivedFrom":[makeQuery(id+"F5.opExtrude","CAP_FACE",FACE,{"disambiguationData":[OSD([sQuery(id+"F0.wireOp",EDGE,"E0"),sQuery(id+"F0.wireOp",EDGE,"E1")])],"isStart":true}),makeQuery(id+"F6.opExtrude","SWEPT_FACE",FACE,{"disambiguationData":[OSD([sQuery(id+"F0.wireOp",EDGE,"E16.9.0")])]})]});
            var Q6;
            Q6=makeQuery(id+"F6.boolean.opBoolean","INTERSECT",EDGE,{"derivedFrom":[makeQuery(id+"F5.opExtrude","CAP_FACE",FACE,{"disambiguationData":[OSD([sQuery(id+"F0.wireOp",EDGE,"E0"),sQuery(id+"F0.wireOp",EDGE,"E1")])],"isStart":true}),makeQuery(id+"F6.opExtrude","SWEPT_FACE",FACE,{"disambiguationData":[OSD([sQuery(id+"F0.wireOp",EDGE,"E16.8.0")])]})]});
            var Q7;
            Q7=makeQuery(id+"F6.boolean.opBoolean","INTERSECT",EDGE,{"derivedFrom":[makeQuery(id+"F5.opExtrude","CAP_FACE",FACE,{"disambiguationData":[OSD([sQuery(id+"F0.wireOp",EDGE,"E0"),sQuery(id+"F0.wireOp",EDGE,"E1")])],"isStart":true}),makeQuery(id+"F6.opExtrude","SWEPT_FACE",FACE,{"disambiguationData":[OSD([sQuery(id+"F0.wireOp",EDGE,"E16.7.0")])]})]});
            var Q8;
            Q8=makeQuery(id+"F6.boolean.opBoolean","INTERSECT",EDGE,{"derivedFrom":[makeQuery(id+"F5.opExtrude","CAP_FACE",FACE,{"disambiguationData":[OSD([sQuery(id+"F0.wireOp",EDGE,"E0"),sQuery(id+"F0.wireOp",EDGE,"E1")])],"isStart":true}),makeQuery(id+"F6.opExtrude","SWEPT_FACE",FACE,{"disambiguationData":[OSD([sQuery(id+"F0.wireOp",EDGE,"E16.6.0")])]})]});
            var Q9;
            Q9=makeQuery(id+"F6.boolean.opBoolean","INTERSECT",EDGE,{"derivedFrom":[makeQuery(id+"F5.opExtrude","CAP_FACE",FACE,{"disambiguationData":[OSD([sQuery(id+"F0.wireOp",EDGE,"E0"),sQuery(id+"F0.wireOp",EDGE,"E1")])],"isStart":true}),makeQuery(id+"F6.opExtrude","SWEPT_FACE",FACE,{"disambiguationData":[OSD([sQuery(id+"F0.wireOp",EDGE,"E16.5.0")])]})]});
            var Q10;
            Q10=makeQuery(id+"F6.boolean.opBoolean","INTERSECT",EDGE,{"derivedFrom":[makeQuery(id+"F5.opExtrude","CAP_FACE",FACE,{"disambiguationData":[OSD([sQuery(id+"F0.wireOp",EDGE,"E0"),sQuery(id+"F0.wireOp",EDGE,"E1")])],"isStart":true}),makeQuery(id+"F6.opExtrude","SWEPT_FACE",FACE,{"disambiguationData":[OSD([sQuery(id+"F0.wireOp",EDGE,"E16.4.0")])]})]});
            var Q11;
            Q11=makeQuery(id+"F6.boolean.opBoolean","INTERSECT",EDGE,{"derivedFrom":[makeQuery(id+"F5.opExtrude","CAP_FACE",FACE,{"disambiguationData":[OSD([sQuery(id+"F0.wireOp",EDGE,"E0"),sQuery(id+"F0.wireOp",EDGE,"E1")])],"isStart":true}),makeQuery(id+"F6.opExtrude","SWEPT_FACE",FACE,{"disambiguationData":[OSD([sQuery(id+"F0.wireOp",EDGE,"E16.3.0")])]})]});
            var Q12;
            Q12=makeQuery(id+"F6.boolean.opBoolean","INTERSECT",EDGE,{"derivedFrom":[makeQuery(id+"F5.opExtrude","CAP_FACE",FACE,{"disambiguationData":[OSD([sQuery(id+"F0.wireOp",EDGE,"E0"),sQuery(id+"F0.wireOp",EDGE,"E1")])],"isStart":true}),makeQuery(id+"F6.opExtrude","SWEPT_FACE",FACE,{"disambiguationData":[OSD([sQuery(id+"F0.wireOp",EDGE,"E16.2.0")])]})]});
            var Q13;
            Q13=makeQuery(id+"F6.boolean.opBoolean","INTERSECT",EDGE,{"derivedFrom":[makeQuery(id+"F5.opExtrude","CAP_FACE",FACE,{"disambiguationData":[OSD([sQuery(id+"F0.wireOp",EDGE,"E0"),sQuery(id+"F0.wireOp",EDGE,"E1")])],"isStart":true}),makeQuery(id+"F6.opExtrude","SWEPT_FACE",FACE,{"disambiguationData":[OSD([sQuery(id+"F0.wireOp",EDGE,"E16.1.0")])]})]});
            var Q14;
            Q14=makeQuery(id+"F6.boolean.opBoolean","INTERSECT",EDGE,{"derivedFrom":[makeQuery(id+"F5.opExtrude","CAP_FACE",FACE,{"disambiguationData":[OSD([sQuery(id+"F0.wireOp",EDGE,"E0"),sQuery(id+"F0.wireOp",EDGE,"E1")])],"isStart":true}),makeQuery(id+"F6.opExtrude","SWEPT_FACE",FACE,{"disambiguationData":[OSD([sQuery(id+"F0.wireOp",EDGE,"E15")])]})]});
            var Q15;
            Q15=makeQuery(id+"F6.boolean.opBoolean","INTERSECT",EDGE,{"derivedFrom":[makeQuery(id+"F5.opExtrude","CAP_FACE",FACE,{"disambiguationData":[OSD([sQuery(id+"F0.wireOp",EDGE,"E0"),sQuery(id+"F0.wireOp",EDGE,"E1")])],"isStart":true}),makeQuery(id+"F6.opExtrude","SWEPT_FACE",FACE,{"disambiguationData":[OSD([sQuery(id+"F0.wireOp",EDGE,"E16.44.0")])]})]});
            var Q16;
            Q16=makeQuery(id+"F6.boolean.opBoolean","INTERSECT",EDGE,{"derivedFrom":[makeQuery(id+"F5.opExtrude","CAP_FACE",FACE,{"disambiguationData":[OSD([sQuery(id+"F0.wireOp",EDGE,"E0"),sQuery(id+"F0.wireOp",EDGE,"E1")])],"isStart":true}),makeQuery(id+"F6.opExtrude","SWEPT_FACE",FACE,{"disambiguationData":[OSD([sQuery(id+"F0.wireOp",EDGE,"E16.43.0")])]})]});
            var Q17;
            Q17=makeQuery(id+"F6.boolean.opBoolean","INTERSECT",EDGE,{"derivedFrom":[makeQuery(id+"F5.opExtrude","CAP_FACE",FACE,{"disambiguationData":[OSD([sQuery(id+"F0.wireOp",EDGE,"E0"),sQuery(id+"F0.wireOp",EDGE,"E1")])],"isStart":true}),makeQuery(id+"F6.opExtrude","SWEPT_FACE",FACE,{"disambiguationData":[OSD([sQuery(id+"F0.wireOp",EDGE,"E16.42.0")])]})]});
            var Q18;
            Q18=makeQuery(id+"F6.boolean.opBoolean","INTERSECT",EDGE,{"derivedFrom":[makeQuery(id+"F5.opExtrude","CAP_FACE",FACE,{"disambiguationData":[OSD([sQuery(id+"F0.wireOp",EDGE,"E0"),sQuery(id+"F0.wireOp",EDGE,"E1")])],"isStart":true}),makeQuery(id+"F6.opExtrude","SWEPT_FACE",FACE,{"disambiguationData":[OSD([sQuery(id+"F0.wireOp",EDGE,"E16.41.0")])]})]});
            var Q19;
            Q19=makeQuery(id+"F6.boolean.opBoolean","INTERSECT",EDGE,{"derivedFrom":[makeQuery(id+"F5.opExtrude","CAP_FACE",FACE,{"disambiguationData":[OSD([sQuery(id+"F0.wireOp",EDGE,"E0"),sQuery(id+"F0.wireOp",EDGE,"E1")])],"isStart":true}),makeQuery(id+"F6.opExtrude","SWEPT_FACE",FACE,{"disambiguationData":[OSD([sQuery(id+"F0.wireOp",EDGE,"E16.40.0")])]})]});
            var Q20;
            Q20=makeQuery(id+"F6.boolean.opBoolean","INTERSECT",EDGE,{"derivedFrom":[makeQuery(id+"F5.opExtrude","CAP_FACE",FACE,{"disambiguationData":[OSD([sQuery(id+"F0.wireOp",EDGE,"E0"),sQuery(id+"F0.wireOp",EDGE,"E1")])],"isStart":true}),makeQuery(id+"F6.opExtrude","SWEPT_FACE",FACE,{"disambiguationData":[OSD([sQuery(id+"F0.wireOp",EDGE,"E16.39.0")])]})]});
            var Q21;
            Q21=makeQuery(id+"F6.boolean.opBoolean","INTERSECT",EDGE,{"derivedFrom":[makeQuery(id+"F5.opExtrude","CAP_FACE",FACE,{"disambiguationData":[OSD([sQuery(id+"F0.wireOp",EDGE,"E0"),sQuery(id+"F0.wireOp",EDGE,"E1")])],"isStart":true}),makeQuery(id+"F6.opExtrude","SWEPT_FACE",FACE,{"disambiguationData":[OSD([sQuery(id+"F0.wireOp",EDGE,"E16.38.0")])]})]});
            var Q22;
            Q22=makeQuery(id+"F6.boolean.opBoolean","INTERSECT",EDGE,{"derivedFrom":[makeQuery(id+"F5.opExtrude","CAP_FACE",FACE,{"disambiguationData":[OSD([sQuery(id+"F0.wireOp",EDGE,"E0"),sQuery(id+"F0.wireOp",EDGE,"E1")])],"isStart":true}),makeQuery(id+"F6.opExtrude","SWEPT_FACE",FACE,{"disambiguationData":[OSD([sQuery(id+"F0.wireOp",EDGE,"E16.37.0")])]})]});
            var Q23;
            Q23=makeQuery(id+"F6.boolean.opBoolean","INTERSECT",EDGE,{"derivedFrom":[makeQuery(id+"F5.opExtrude","CAP_FACE",FACE,{"disambiguationData":[OSD([sQuery(id+"F0.wireOp",EDGE,"E0"),sQuery(id+"F0.wireOp",EDGE,"E1")])],"isStart":true}),makeQuery(id+"F6.opExtrude","SWEPT_FACE",FACE,{"disambiguationData":[OSD([sQuery(id+"F0.wireOp",EDGE,"E16.36.0")])]})]});
            var Q24;
            Q24=makeQuery(id+"F6.boolean.opBoolean","INTERSECT",EDGE,{"derivedFrom":[makeQuery(id+"F5.opExtrude","CAP_FACE",FACE,{"disambiguationData":[OSD([sQuery(id+"F0.wireOp",EDGE,"E0"),sQuery(id+"F0.wireOp",EDGE,"E1")])],"isStart":true}),makeQuery(id+"F6.opExtrude","SWEPT_FACE",FACE,{"disambiguationData":[OSD([sQuery(id+"F0.wireOp",EDGE,"E16.35.0")])]})]});
            var Q25;
            Q25=makeQuery(id+"F6.boolean.opBoolean","INTERSECT",EDGE,{"derivedFrom":[makeQuery(id+"F5.opExtrude","CAP_FACE",FACE,{"disambiguationData":[OSD([sQuery(id+"F0.wireOp",EDGE,"E0"),sQuery(id+"F0.wireOp",EDGE,"E1")])],"isStart":true}),makeQuery(id+"F6.opExtrude","SWEPT_FACE",FACE,{"disambiguationData":[OSD([sQuery(id+"F0.wireOp",EDGE,"E16.34.0")])]})]});
            var Q26;
            Q26=makeQuery(id+"F6.boolean.opBoolean","INTERSECT",EDGE,{"derivedFrom":[makeQuery(id+"F5.opExtrude","CAP_FACE",FACE,{"disambiguationData":[OSD([sQuery(id+"F0.wireOp",EDGE,"E0"),sQuery(id+"F0.wireOp",EDGE,"E1")])],"isStart":true}),makeQuery(id+"F6.opExtrude","SWEPT_FACE",FACE,{"disambiguationData":[OSD([sQuery(id+"F0.wireOp",EDGE,"E16.33.0")])]})]});
            var Q27;
            Q27=makeQuery(id+"F6.boolean.opBoolean","INTERSECT",EDGE,{"derivedFrom":[makeQuery(id+"F5.opExtrude","CAP_FACE",FACE,{"disambiguationData":[OSD([sQuery(id+"F0.wireOp",EDGE,"E0"),sQuery(id+"F0.wireOp",EDGE,"E1")])],"isStart":true}),makeQuery(id+"F6.opExtrude","SWEPT_FACE",FACE,{"disambiguationData":[OSD([sQuery(id+"F0.wireOp",EDGE,"E16.32.0")])]})]});
            var Q28;
            Q28=makeQuery(id+"F6.boolean.opBoolean","INTERSECT",EDGE,{"derivedFrom":[makeQuery(id+"F5.opExtrude","CAP_FACE",FACE,{"disambiguationData":[OSD([sQuery(id+"F0.wireOp",EDGE,"E0"),sQuery(id+"F0.wireOp",EDGE,"E1")])],"isStart":true}),makeQuery(id+"F6.opExtrude","SWEPT_FACE",FACE,{"disambiguationData":[OSD([sQuery(id+"F0.wireOp",EDGE,"E16.31.0")])]})]});
            var Q29;
            Q29=makeQuery(id+"F6.boolean.opBoolean","INTERSECT",EDGE,{"derivedFrom":[makeQuery(id+"F5.opExtrude","CAP_FACE",FACE,{"disambiguationData":[OSD([sQuery(id+"F0.wireOp",EDGE,"E0"),sQuery(id+"F0.wireOp",EDGE,"E1")])],"isStart":true}),makeQuery(id+"F6.opExtrude","SWEPT_FACE",FACE,{"disambiguationData":[OSD([sQuery(id+"F0.wireOp",EDGE,"E16.30.0")])]})]});
            var Q30;
            Q30=makeQuery(id+"F6.boolean.opBoolean","INTERSECT",EDGE,{"derivedFrom":[makeQuery(id+"F5.opExtrude","CAP_FACE",FACE,{"disambiguationData":[OSD([sQuery(id+"F0.wireOp",EDGE,"E0"),sQuery(id+"F0.wireOp",EDGE,"E1")])],"isStart":true}),makeQuery(id+"F6.opExtrude","SWEPT_FACE",FACE,{"disambiguationData":[OSD([sQuery(id+"F0.wireOp",EDGE,"E16.29.0")])]})]});
            var Q31;
            Q31=makeQuery(id+"F6.boolean.opBoolean","INTERSECT",EDGE,{"derivedFrom":[makeQuery(id+"F5.opExtrude","CAP_FACE",FACE,{"disambiguationData":[OSD([sQuery(id+"F0.wireOp",EDGE,"E0"),sQuery(id+"F0.wireOp",EDGE,"E1")])],"isStart":true}),makeQuery(id+"F6.opExtrude","SWEPT_FACE",FACE,{"disambiguationData":[OSD([sQuery(id+"F0.wireOp",EDGE,"E16.28.0")])]})]});
            var Q32;
            Q32=makeQuery(id+"F6.boolean.opBoolean","INTERSECT",EDGE,{"derivedFrom":[makeQuery(id+"F5.opExtrude","CAP_FACE",FACE,{"disambiguationData":[OSD([sQuery(id+"F0.wireOp",EDGE,"E0"),sQuery(id+"F0.wireOp",EDGE,"E1")])],"isStart":true}),makeQuery(id+"F6.opExtrude","SWEPT_FACE",FACE,{"disambiguationData":[OSD([sQuery(id+"F0.wireOp",EDGE,"E16.27.0")])]})]});
            var Q33;
            Q33=makeQuery(id+"F6.boolean.opBoolean","INTERSECT",EDGE,{"derivedFrom":[makeQuery(id+"F5.opExtrude","CAP_FACE",FACE,{"disambiguationData":[OSD([sQuery(id+"F0.wireOp",EDGE,"E0"),sQuery(id+"F0.wireOp",EDGE,"E1")])],"isStart":true}),makeQuery(id+"F6.opExtrude","SWEPT_FACE",FACE,{"disambiguationData":[OSD([sQuery(id+"F0.wireOp",EDGE,"E16.26.0")])]})]});
            var Q34;
            Q34=makeQuery(id+"F6.boolean.opBoolean","INTERSECT",EDGE,{"derivedFrom":[makeQuery(id+"F5.opExtrude","CAP_FACE",FACE,{"disambiguationData":[OSD([sQuery(id+"F0.wireOp",EDGE,"E0"),sQuery(id+"F0.wireOp",EDGE,"E1")])],"isStart":true}),makeQuery(id+"F6.opExtrude","SWEPT_FACE",FACE,{"disambiguationData":[OSD([sQuery(id+"F0.wireOp",EDGE,"E16.25.0")])]})]});
            var Q35;
            Q35=makeQuery(id+"F6.boolean.opBoolean","INTERSECT",EDGE,{"derivedFrom":[makeQuery(id+"F5.opExtrude","CAP_FACE",FACE,{"disambiguationData":[OSD([sQuery(id+"F0.wireOp",EDGE,"E0"),sQuery(id+"F0.wireOp",EDGE,"E1")])],"isStart":true}),makeQuery(id+"F6.opExtrude","SWEPT_FACE",FACE,{"disambiguationData":[OSD([sQuery(id+"F0.wireOp",EDGE,"E16.24.0")])]})]});
            var Q36;
            Q36=makeQuery(id+"F6.boolean.opBoolean","INTERSECT",EDGE,{"derivedFrom":[makeQuery(id+"F5.opExtrude","CAP_FACE",FACE,{"disambiguationData":[OSD([sQuery(id+"F0.wireOp",EDGE,"E0"),sQuery(id+"F0.wireOp",EDGE,"E1")])],"isStart":true}),makeQuery(id+"F6.opExtrude","SWEPT_FACE",FACE,{"disambiguationData":[OSD([sQuery(id+"F0.wireOp",EDGE,"E16.23.0")])]})]});
            var Q37;
            Q37=makeQuery(id+"F6.boolean.opBoolean","INTERSECT",EDGE,{"derivedFrom":[makeQuery(id+"F5.opExtrude","CAP_FACE",FACE,{"disambiguationData":[OSD([sQuery(id+"F0.wireOp",EDGE,"E0"),sQuery(id+"F0.wireOp",EDGE,"E1")])],"isStart":true}),makeQuery(id+"F6.opExtrude","SWEPT_FACE",FACE,{"disambiguationData":[OSD([sQuery(id+"F0.wireOp",EDGE,"E16.22.0")])]})]});
            var Q38;
            Q38=makeQuery(id+"F6.boolean.opBoolean","INTERSECT",EDGE,{"derivedFrom":[makeQuery(id+"F5.opExtrude","CAP_FACE",FACE,{"disambiguationData":[OSD([sQuery(id+"F0.wireOp",EDGE,"E0"),sQuery(id+"F0.wireOp",EDGE,"E1")])],"isStart":true}),makeQuery(id+"F6.opExtrude","SWEPT_FACE",FACE,{"disambiguationData":[OSD([sQuery(id+"F0.wireOp",EDGE,"E16.21.0")])]})]});
            var Q39;
            Q39=makeQuery(id+"F6.boolean.opBoolean","INTERSECT",EDGE,{"derivedFrom":[makeQuery(id+"F5.opExtrude","CAP_FACE",FACE,{"disambiguationData":[OSD([sQuery(id+"F0.wireOp",EDGE,"E0"),sQuery(id+"F0.wireOp",EDGE,"E1")])],"isStart":true}),makeQuery(id+"F6.opExtrude","SWEPT_FACE",FACE,{"disambiguationData":[OSD([sQuery(id+"F0.wireOp",EDGE,"E16.20.0")])]})]});
            var Q40;
            Q40=makeQuery(id+"F6.boolean.opBoolean","INTERSECT",EDGE,{"derivedFrom":[makeQuery(id+"F5.opExtrude","CAP_FACE",FACE,{"disambiguationData":[OSD([sQuery(id+"F0.wireOp",EDGE,"E0"),sQuery(id+"F0.wireOp",EDGE,"E1")])],"isStart":true}),makeQuery(id+"F6.opExtrude","SWEPT_FACE",FACE,{"disambiguationData":[OSD([sQuery(id+"F0.wireOp",EDGE,"E16.19.0")])]})]});
            var Q41;
            Q41=makeQuery(id+"F6.boolean.opBoolean","INTERSECT",EDGE,{"derivedFrom":[makeQuery(id+"F5.opExtrude","CAP_FACE",FACE,{"disambiguationData":[OSD([sQuery(id+"F0.wireOp",EDGE,"E0"),sQuery(id+"F0.wireOp",EDGE,"E1")])],"isStart":true}),makeQuery(id+"F6.opExtrude","SWEPT_FACE",FACE,{"disambiguationData":[OSD([sQuery(id+"F0.wireOp",EDGE,"E16.18.0")])]})]});
            var Q42;
            Q42=makeQuery(id+"F6.boolean.opBoolean","INTERSECT",EDGE,{"derivedFrom":[makeQuery(id+"F5.opExtrude","CAP_FACE",FACE,{"disambiguationData":[OSD([sQuery(id+"F0.wireOp",EDGE,"E0"),sQuery(id+"F0.wireOp",EDGE,"E1")])],"isStart":true}),makeQuery(id+"F6.opExtrude","SWEPT_FACE",FACE,{"disambiguationData":[OSD([sQuery(id+"F0.wireOp",EDGE,"E16.17.0")])]})]});
            var Q43;
            Q43=makeQuery(id+"F6.boolean.opBoolean","INTERSECT",EDGE,{"derivedFrom":[makeQuery(id+"F5.opExtrude","CAP_FACE",FACE,{"disambiguationData":[OSD([sQuery(id+"F0.wireOp",EDGE,"E0"),sQuery(id+"F0.wireOp",EDGE,"E1")])],"isStart":true}),makeQuery(id+"F6.opExtrude","SWEPT_FACE",FACE,{"disambiguationData":[OSD([sQuery(id+"F0.wireOp",EDGE,"E16.16.0")])]})]});
            var Q44;
            Q44=makeQuery(id+"F6.boolean.opBoolean","INTERSECT",EDGE,{"derivedFrom":[makeQuery(id+"F5.opExtrude","CAP_FACE",FACE,{"disambiguationData":[OSD([sQuery(id+"F0.wireOp",EDGE,"E0"),sQuery(id+"F0.wireOp",EDGE,"E1")])],"isStart":true}),makeQuery(id+"F6.opExtrude","SWEPT_FACE",FACE,{"disambiguationData":[OSD([sQuery(id+"F0.wireOp",EDGE,"E16.15.0")])]})]});
            fillet(context, id + "F7", {"entities" : qUnion([Q0, Q1, Q2, Q3, Q4, Q5, Q6, Q7, Q8, Q9, Q10, Q11, Q12, Q13, Q14, Q15, Q16, Q17, Q18, Q19, Q20, Q21, Q22, Q23, Q24, Q25, Q26, Q27, Q28, Q29, Q30, Q31, Q32, Q33, Q34, Q35, Q36, Q37, Q38, Q39, Q40, Q41, Q42, Q43, Q44]), "radius" : 1 * mm, "tangentPropagation" : true, "allowEdgeOverflow" : false});
        }
        {
            var Q0;
            {var subQ0=sQuery(id+"F0.wireOp",EDGE,"E0");Q0=makeQuery(id+"F6.opExtrude","CAP_EDGE",EDGE,{"disambiguationData":[OSD([subQ0]),TDD([makeQuery(id+"F0.imprint","IMPRINT",EDGE,{"disambiguationData":[TD([[makeQuery(id+"F0.imprint","INTERSECT",VERTEX,{"disambiguationData":[OD(1.0)],"derivedFrom":[subQ0,sQuery(id+"F0.wireOp",EDGE,"E16.17.0")]}),-1.0]])],"derivedFrom":subQ0})])],"isStart":true});}
            var Q1;
            Q1=makeQuery(id+"F4.opExtrude","CAP_EDGE",EDGE,{"disambiguationData":[OSD([sQuery(id+"F0.wireOp",EDGE,"E1")])],"isStart":false});
            var Q2;
            Q2=makeQuery(id+"F4.opExtrude","CAP_EDGE",EDGE,{"disambiguationData":[OSD([sQuery(id+"F0.wireOp",EDGE,"E2")])],"isStart":false});
            var Q3;
            Q3=makeQuery(id+"F4.opExtrude","CAP_EDGE",EDGE,{"disambiguationData":[OSD([sQuery(id+"F0.wireOp",EDGE,"E4")])],"isStart":false});
            var Q4;
            Q4=makeQuery(id+"F1.opExtrude","CAP_EDGE",EDGE,{"disambiguationData":[OSD([sQuery(id+"F0.wireOp",EDGE,"E4")])],"isStart":false});
            chamfer(context, id + "F8", {"entities" : qUnion([Q0, Q1, Q2, Q3, Q4]), "width" : 0.8 * mm, "tangentPropagation" : true});
        }
    });
